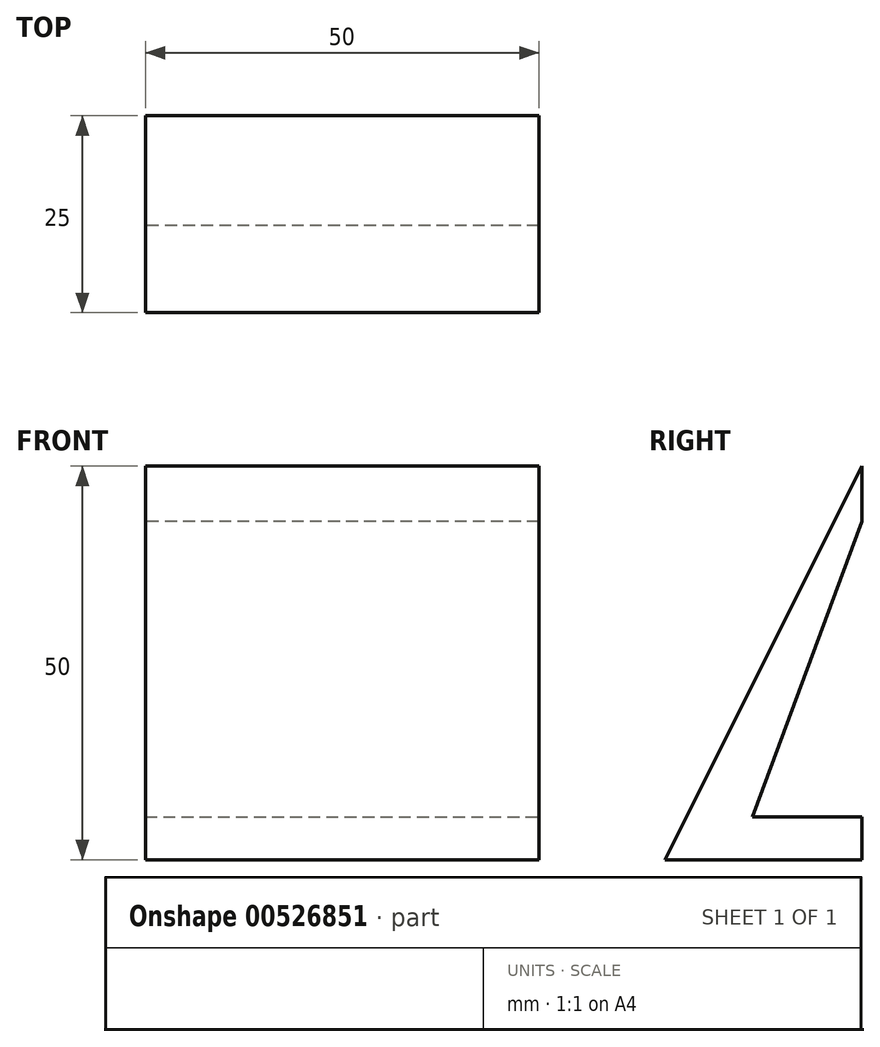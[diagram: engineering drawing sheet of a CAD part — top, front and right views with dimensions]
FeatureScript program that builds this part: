
annotation { "Feature Type Name" : "Feature", "Feature Type Description" : "" }
export const myFeature = defineFeature(function(context is Context, id is Id, definition is map)
    precondition{}
    {
        {
            var Q0;
            Q0=qCreatedBy(makeId("Right.planeOp"),FACE);
            var sketch = newSketch(context, id + "F0", { "sketchPlane" : qUnion([Q0])});
            skLineSegment(sketch, "E0", {"start": v(0, 0) * mm, "end": v(25, 0) * mm});
            skLineSegment(sketch, "E1", {"start": v(25, 0) * mm, "end": v(0, 0) * mm});
            skLineSegment(sketch, "E2", {"start": v(0, 0) * mm, "end": v(-25, 0) * mm});
            skLineSegment(sketch, "E3", {"start": v(0, 0) * mm, "end": v(0, 50) * mm});
            skLineSegment(sketch, "E4", {"start": v(0, 50) * mm, "end": v(-25, 0) * mm});
            skLineSegment(sketch, "E5", {"start": v(0, 50) * mm, "end": v(25, 0) * mm});
            skSolve(sketch);
        }
        {
            var Q0;
            Q0=makeQuery(id+"F0.imprint","IMPRINT",FACE,{"disambiguationData":[TD([[makeQuery(id+"F0.imprint","IMPRINT",EDGE,{"derivedFrom":sQuery(id+"F0.wireOp",EDGE,"E2")}),-1.0]])]});
            var Q1;
            Q1=makeQuery(id+"F0.imprint","IMPRINT",FACE,{"disambiguationData":[TD([[makeQuery(id+"F0.imprint","IMPRINT",EDGE,{"derivedFrom":sQuery(id+"F0.wireOp",EDGE,"E1")}),-1.0]])]});
            extrude(context, id + "F1", {"entities" : qUnion([Q0, Q1]), "depth" : 25 * mm, "offsetDistance" : 25 * mm});
        }
        {
            var Q0;
            Q0=makeQuery(id+"F1.opExtrude","CAP_FACE",FACE,{"disambiguationData":[OSD([sQuery(id+"F0.wireOp",EDGE,"E1"),sQuery(id+"F0.wireOp",EDGE,"E2"),sQuery(id+"F0.wireOp",EDGE,"E4"),sQuery(id+"F0.wireOp",EDGE,"E5")])],"isStart":true});
            extrude(context, id + "F2", {"entities" : qUnion([Q0]), "operationType" : NewBodyOperationType.ADD, "depth" : 25 * mm, "offsetDistance" : 25 * mm});
        }
        {
            var Q0;
            Q0=makeQuery(id+"F2.opExtrude","CAP_FACE",FACE,{"disambiguationData":[OSD([sQuery(id+"F0.wireOp",EDGE,"E1"),sQuery(id+"F0.wireOp",EDGE,"E2"),sQuery(id+"F0.wireOp",EDGE,"E4"),sQuery(id+"F0.wireOp",EDGE,"E5")])],"isStart":false});
            var sketch = newSketch(context, id + "F3", { "sketchPlane" : qUnion([Q0])});
            skLineSegment(sketch, "E6", {"start": v(0, 5.46) * mm, "end": v(0, 42.96) * mm});
            skLineSegment(sketch, "E7", {"start": v(0, 42.96) * mm, "end": v(13.92, 5.46) * mm});
            skLineSegment(sketch, "E8", {"start": v(13.92, 5.46) * mm, "end": v(0, 5.46) * mm});
            skLineSegment(sketch, "E9.MirrorCS", {"start": v(0, 42.96) * mm, "end": v(-13.92, 5.46) * mm});
            skLineSegment(sketch, "E10.MirrorCS", {"start": v(-13.92, 5.46) * mm, "end": v(0, 5.46) * mm});
            skSolve(sketch);
        }
        {
            var Q0;
            Q0=makeQuery(id+"F3.imprint","IMPRINT",FACE,{"disambiguationData":[TD([[makeQuery(id+"F3.imprint","IMPRINT",EDGE,{"derivedFrom":sQuery(id+"F3.wireOp",EDGE,"E6")}),1.0]])]});
            var Q1;
            Q1=makeQuery(id+"F3.imprint","IMPRINT",FACE,{"disambiguationData":[TD([[makeQuery(id+"F3.imprint","IMPRINT",EDGE,{"derivedFrom":sQuery(id+"F3.wireOp",EDGE,"E6")}),-1.0]])]});
            extrude(context, id + "F4", {"entities" : qUnion([Q0, Q1]), "operationType" : NewBodyOperationType.REMOVE, "oppositeDirection" : true, "depth" : 25 * mm, "offsetDistance" : 25 * mm});
        }
        {
            var Q0;
            Q0=makeQuery(id+"F1.opExtrude","CAP_FACE",FACE,{"disambiguationData":[OSD([sQuery(id+"F0.wireOp",EDGE,"E1"),sQuery(id+"F0.wireOp",EDGE,"E2"),sQuery(id+"F0.wireOp",EDGE,"E4"),sQuery(id+"F0.wireOp",EDGE,"E5")])],"isStart":false});
            var Q1;
            {var subQ0=sQuery(id+"F0.wireOp",EDGE,"E5");Q1=makeQuery(id+"F2.boolean.opBoolean","MERGE",FACE,{"derivedFrom":[makeQuery(id+"F1.opExtrude","SWEPT_FACE",FACE,{"disambiguationData":[OSD([subQ0])]}),makeQuery(id+"F2.opExtrude","SWEPT_FACE",FACE,{"disambiguationData":[OSD([subQ0])]})]});}
            var Q2;
            Q2=makeQuery(id+"F4.boolean.opBoolean","COPY",FACE,{"derivedFrom":makeQuery(id+"F4.opExtrude","CAP_FACE",FACE,{"disambiguationData":[OSD([sQuery(id+"F3.wireOp",EDGE,"E7"),sQuery(id+"F3.wireOp",EDGE,"E8"),sQuery(id+"F3.wireOp",EDGE,"E9.MirrorCS"),sQuery(id+"F3.wireOp",EDGE,"E10.MirrorCS")])],"isStart":false})});
            extrude(context, id + "F5", {"entities" : qUnion([Q0, Q1, Q2]), "operationType" : NewBodyOperationType.REMOVE, "depth" : 25 * mm, "offsetDistance" : 25 * mm});
        }
    });
